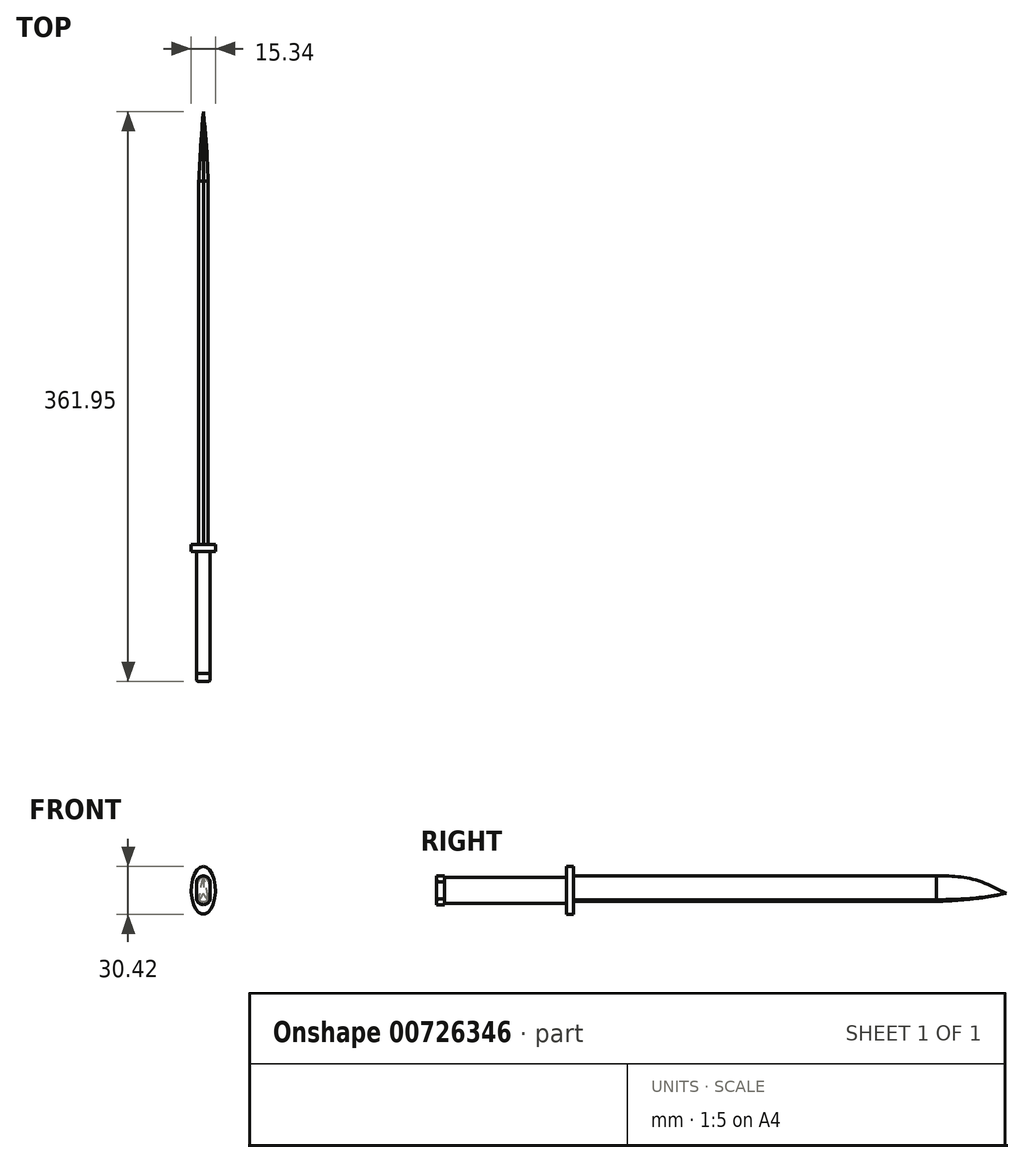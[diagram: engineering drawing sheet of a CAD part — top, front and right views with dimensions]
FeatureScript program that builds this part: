
annotation { "Feature Type Name" : "Feature", "Feature Type Description" : "" }
export const myFeature = defineFeature(function(context is Context, id is Id, definition is map)
    precondition{}
    {
        {
            var Q0;
            Q0=qCreatedBy(makeId("Front.planeOp"),FACE);
            var sketch = newSketch(context, id + "F0", { "sketchPlane" : qUnion([Q0])});
            skEllipse(sketch, "E0", {"center": v(0, 0) * mm, "majorRadius": 15.2 * mm, "minorRadius": 7.67 * mm, "majorAxis": v(0, 1)});
            skSolve(sketch);
        }
        {
            var Q0;
            Q0=makeQuery(id+"F0.imprint","IMPRINT",FACE,{"disambiguationData":[TD([[makeQuery(id+"F0.imprint","IMPRINT",EDGE,{"derivedFrom":sQuery(id+"F0.wireOp",EDGE,"E0")}),1.0]])]});
            extrude(context, id + "F1", {"entities" : qUnion([Q0]), "oppositeDirection" : true, "depth" : 4.57 * mm, "offsetDistance" : 25.4 * mm});
        }
        {
            var Q0;
            Q0=makeQuery(id+"F1.opExtrude","CAP_FACE",FACE,{"disambiguationData":[OSD([sQuery(id+"F0.wireOp",EDGE,"E0")])],"isStart":false});
            var sketch = newSketch(context, id + "F2", { "sketchPlane" : qUnion([Q0])});
            skArc(sketch, "E1", {"start": v(0, 9.3) * mm, "mid": v(-2, 1.75) * mm, "end": v(-3.04, -6) * mm});
            skArc(sketch, "E2", {"start": v(2.86, -6.18) * mm, "mid": v(1.85, 1.64) * mm, "end": v(0, 9.3) * mm});
            skArc(sketch, "E3", {"start": v(-3.04, -6) * mm, "mid": v(-0.12, -7.12) * mm, "end": v(2.86, -6.18) * mm});
            skSolve(sketch);
        }
        {
            var Q0;
            Q0=makeQuery(id+"F2.imprint","IMPRINT",FACE,{"disambiguationData":[TD([[makeQuery(id+"F2.imprint","IMPRINT",EDGE,{"derivedFrom":sQuery(id+"F2.wireOp",EDGE,"E1")}),1.0]])]});
            extrude(context, id + "F3", {"entities" : qUnion([Q0]), "operationType" : NewBodyOperationType.ADD, "depth" : 230.63 * mm, "offsetDistance" : 25.4 * mm});
        }
        {
            var Q0;
            Q0=makeQuery(id+"F1.opExtrude","CAP_FACE",FACE,{"disambiguationData":[OSD([sQuery(id+"F0.wireOp",EDGE,"E0")])],"isStart":true});
            var sketch = newSketch(context, id + "F4", { "sketchPlane" : qUnion([Q0])});
            skEllipse(sketch, "E4", {"center": v(0, 0) * mm, "majorRadius": 8.39 * mm, "minorRadius": 4.41 * mm, "majorAxis": v(0, 1)});
            skSolve(sketch);
        }
        {
            var Q0;
            Q0=makeQuery(id+"F4.imprint","IMPRINT",FACE,{"disambiguationData":[TD([[makeQuery(id+"F4.imprint","IMPRINT",EDGE,{"derivedFrom":sQuery(id+"F4.wireOp",EDGE,"E4")}),1.0]])]});
            extrude(context, id + "F5", {"entities" : qUnion([Q0]), "operationType" : NewBodyOperationType.ADD, "depth" : 82.55 * mm, "offsetDistance" : 25.4 * mm});
        }
        {
            var Q0;
            Q0=makeQuery(id+"F5.opExtrude","CAP_FACE",FACE,{"disambiguationData":[OSD([sQuery(id+"F4.wireOp",EDGE,"E4")])],"isStart":false});
            var sketch = newSketch(context, id + "F6", { "sketchPlane" : qUnion([Q0])});
            skLineSegment(sketch, "E5", {"start": v(-4.41, 5.51) * mm, "end": v(-4.41, -5.27) * mm});
            skPoint(sketch, "E5.startSnap0", {"position": v(-4.41, 0) * mm});
            skLineSegment(sketch, "E6", {"start": v(4.41, 5.42) * mm, "end": v(4.41, -5.46) * mm});
            skArc(sketch, "E7", {"start": v(4.41, 5.42) * mm, "mid": v(0.04, 9.14) * mm, "end": v(-4.41, 5.51) * mm});
            skArc(sketch, "E8", {"start": v(-4.41, -5.27) * mm, "mid": v(-0.08, -9.07) * mm, "end": v(4.41, -5.46) * mm});
            skPoint(sketch, "E9.orphan", {"position": v(4.41, 8.46) * mm});
            skPoint(sketch, "E10.orphan", {"position": v(-4.41, 8.46) * mm});
            skPoint(sketch, "E11.orphan", {"position": v(4.41, -8.96) * mm});
            skPoint(sketch, "E12.orphan", {"position": v(-4.41, -8.96) * mm});
            skSolve(sketch);
        }
        {
            var Q0;
            Q0=makeQuery(id+"F6.imprint","IMPRINT",FACE,{"disambiguationData":[TD([[makeQuery(id+"F6.imprint","IMPRINT",EDGE,{"derivedFrom":makeQuery(id+"F5.opExtrude","CAP_EDGE",EDGE,{"disambiguationData":[OSD([sQuery(id+"F4.wireOp",EDGE,"E4")])],"isStart":false})}),1.0]])]});
            var Q1;
            Q1=makeQuery(id+"F6.imprint","IMPRINT",FACE,{"disambiguationData":[TD([[makeQuery(id+"F6.imprint","IMPRINT",EDGE,{"derivedFrom":sQuery(id+"F6.wireOp",EDGE,"E6")}),-1.0]])]});
            extrude(context, id + "F7", {"entities" : qUnion([Q0, Q1]), "operationType" : NewBodyOperationType.ADD, "oppositeDirection" : true, "depth" : 5.08 * mm, "offsetDistance" : 25.4 * mm});
        }
        {
            var Q0;
            Q0=makeQuery(id+"F7.opExtrude","CAP_EDGE",EDGE,{"disambiguationData":[OSD([sQuery(id+"F6.wireOp",EDGE,"E6")])],"isStart":true});
            fillet(context, id + "F8", {"entities" : qUnion([Q0]), "radius" : 1.29 * mm, "tangentPropagation" : true, "allowEdgeOverflow" : false});
        }
        {
            var Q0;
            Q0=makeQuery(id+"F7.opExtrude","CAP_EDGE",EDGE,{"disambiguationData":[OSD([sQuery(id+"F6.wireOp",EDGE,"E5")])],"isStart":true});
            fillet(context, id + "F9", {"entities" : qUnion([Q0]), "radius" : 1.3 * mm, "tangentPropagation" : true, "allowEdgeOverflow" : false});
        }
        {
            var Q0;
            Q0=makeQuery(id+"F3.opExtrude","CAP_FACE",FACE,{"disambiguationData":[OSD([sQuery(id+"F2.wireOp",EDGE,"E1"),sQuery(id+"F2.wireOp",EDGE,"E2"),sQuery(id+"F2.wireOp",EDGE,"E3")])],"isStart":false});
            var sketch = newSketch(context, id + "F10", { "sketchPlane" : qUnion([Q0])});
            skArc(sketch, "E13", {"start": v(0, 9.3) * mm, "mid": v(-1.9, 1.73) * mm, "end": v(-3.04, -6) * mm});
            skArc(sketch, "E14", {"start": v(2.86, -6.18) * mm, "mid": v(1.85, 1.64) * mm, "end": v(0, 9.3) * mm});
            skArc(sketch, "E15", {"start": v(-3.04, -6) * mm, "mid": v(-0.13, -7.19) * mm, "end": v(2.86, -6.18) * mm});
            skSolve(sketch);
        }
        {
            var Q0;
            Q0=makeQuery(id+"F10.imprint","IMPRINT",FACE,{"disambiguationData":[TD([[makeQuery(id+"F10.imprint","IMPRINT",EDGE,{"derivedFrom":sQuery(id+"F10.wireOp",EDGE,"E13")}),1.0]])]});
            cPlane(context, id + "F11", {"entities" : qUnion([Q0]), "cplaneType" : CPlaneType.OFFSET, "offset" : 44.2 * mm, "width" : 152.4 * mm, "height" : 152.4 * mm});
        }
        {
            var Q0;
            Q0=qCreatedBy(id+"F11.planeOp",FACE);
            var sketch = newSketch(context, id + "F12", { "sketchPlane" : qUnion([Q0])});
            skPoint(sketch, "E16", {"position": v(0, -1.97) * mm});
            skSolve(sketch);
        }
        {
            var Q0;
            Q0=makeQuery(id+"F10.imprint","IMPRINT",FACE,{"disambiguationData":[TD([[makeQuery(id+"F10.imprint","IMPRINT",EDGE,{"derivedFrom":sQuery(id+"F10.wireOp",EDGE,"E13")}),1.0]])]});
            cPlane(context, id + "F13", {"entities" : qUnion([Q0]), "cplaneType" : CPlaneType.OFFSET, "offset" : 26.42 * mm, "width" : 152.4 * mm, "height" : 152.4 * mm});
        }
        {
            var Q0;
            Q0=qCreatedBy(id+"F13.planeOp",FACE);
            var sketch = newSketch(context, id + "F14", { "sketchPlane" : qUnion([Q0])});
            skArc(sketch, "E17", {"start": v(0, 6.12) * mm, "mid": v(-1.2, 0.8) * mm, "end": v(-1.76, -4.62) * mm});
            skArc(sketch, "E18", {"start": v(1.42, -4.62) * mm, "mid": v(0.99, 0.79) * mm, "end": v(0, 6.12) * mm});
            skArc(sketch, "E19", {"start": v(-1.76, -4.62) * mm, "mid": v(-0.17, -5.02) * mm, "end": v(1.42, -4.62) * mm});
            skSolve(sketch);
        }
        {
            var Q1;
            Q1=makeQuery(id+"F10.imprint","IMPRINT",FACE,{"disambiguationData":[TD([[makeQuery(id+"F10.imprint","IMPRINT",EDGE,{"derivedFrom":sQuery(id+"F10.wireOp",EDGE,"E13")}),1.0]])]});
            var Q2;
            Q2=makeQuery(id+"F14.imprint","IMPRINT",FACE,{"disambiguationData":[TD([[makeQuery(id+"F14.imprint","IMPRINT",EDGE,{"derivedFrom":sQuery(id+"F14.wireOp",EDGE,"E17")}),1.0]])]});
            var Q3;
            Q3=sQuery(id+"F12.wireOp",VERTEX,"E16");
            loft(context, id + "F15", {"operationType" : NewBodyOperationType.ADD, "sheetProfilesArray" : [{ "sheetProfileEntities" : qUnion([Q1]) }, { "sheetProfileEntities" : qUnion([Q2]) }, { "sheetProfileEntities" : qUnion([Q3]) }]});
        }
    });
